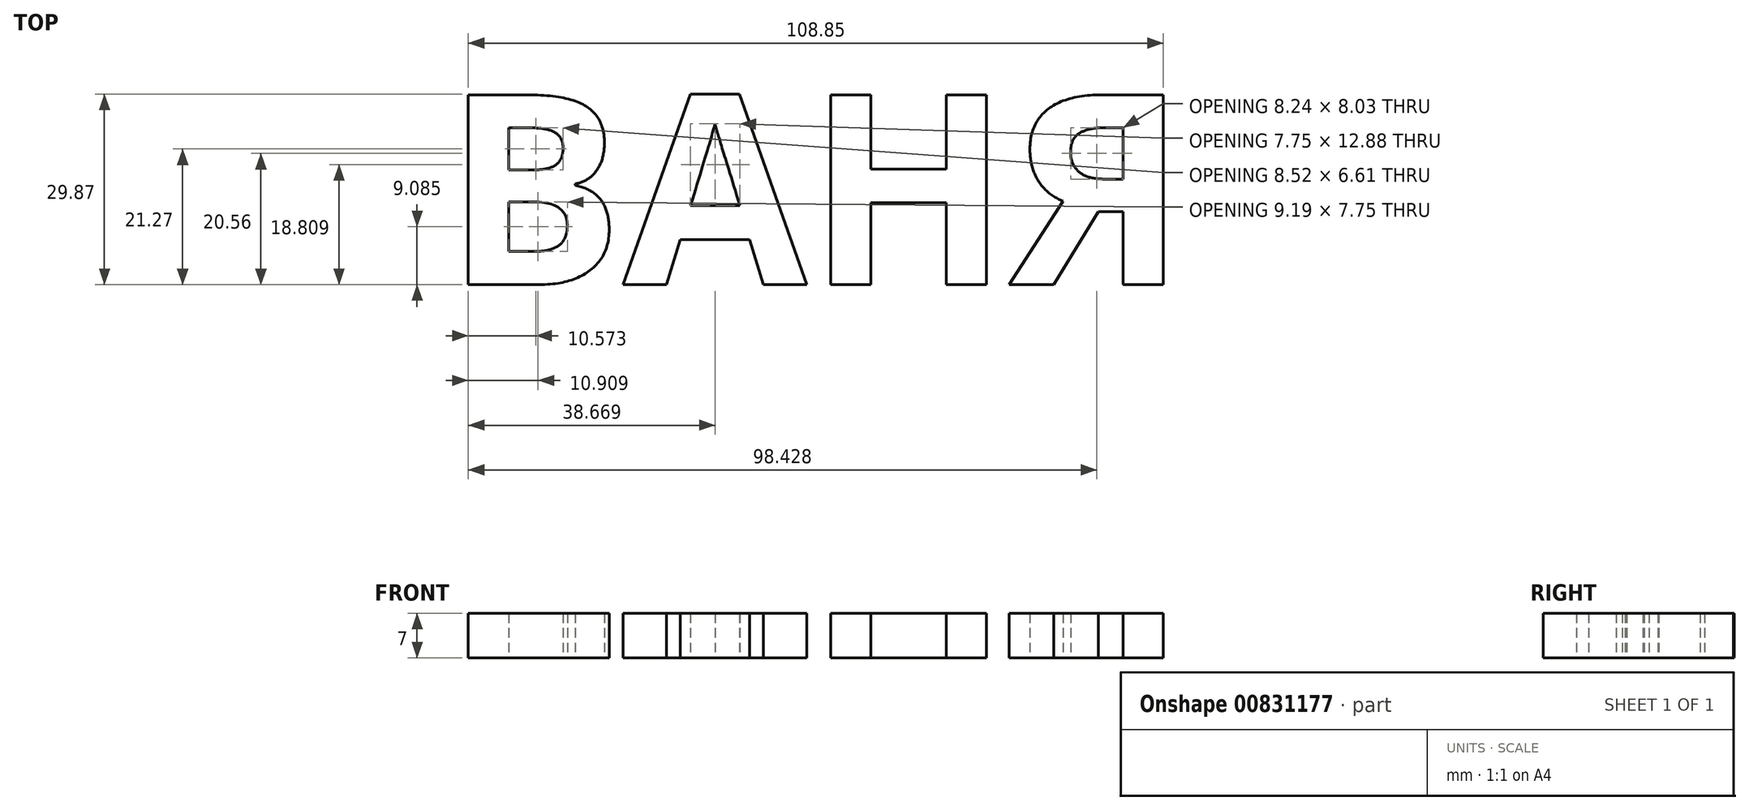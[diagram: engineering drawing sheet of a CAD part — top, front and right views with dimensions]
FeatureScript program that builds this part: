
annotation { "Feature Type Name" : "Feature", "Feature Type Description" : "" }
export const myFeature = defineFeature(function(context is Context, id is Id, definition is map)
    precondition{}
    {
        {
            var Q0;
            Q0=qCreatedBy(makeId("Top.planeOp"),FACE);
            var sketch = newSketch(context, id + "F0", { "sketchPlane" : qUnion([Q0])});
            skText(sketch, "E0", { "text": "ВАНЯ\n", "fontName": "OpenSans-Bold.ttf"});
            const initialGuessF0  = {"E0": [-0.03325, -0.01518, 1, 0, 0.03]};
            skSetInitialGuess(sketch, initialGuessF0);
            skSolve(sketch);
        }
        {
            var Q0;
            Q0=makeQuery(id+"F0.imprint","IMPRINT",FACE,{"disambiguationData":[TD([[makeQuery(id+"F0.imprint","IMPRINT",EDGE,{"derivedFrom":sQuery(id+"F0.wireOp",EDGE,"E0.sketch_text.stroke-49")}),-1.0]])]});
            var Q1;
            Q1=makeQuery(id+"F0.imprint","IMPRINT",FACE,{"disambiguationData":[TD([[makeQuery(id+"F0.imprint","IMPRINT",EDGE,{"derivedFrom":sQuery(id+"F0.wireOp",EDGE,"E0.sketch_text.stroke-37")}),-1.0]])]});
            var Q2;
            Q2=makeQuery(id+"F0.imprint","IMPRINT",FACE,{"disambiguationData":[TD([[makeQuery(id+"F0.imprint","IMPRINT",EDGE,{"derivedFrom":sQuery(id+"F0.wireOp",EDGE,"E0.sketch_text.stroke-25")}),-1.0]])]});
            var Q3;
            Q3=makeQuery(id+"F0.imprint","IMPRINT",FACE,{"disambiguationData":[TD([[makeQuery(id+"F0.imprint","IMPRINT",EDGE,{"derivedFrom":sQuery(id+"F0.wireOp",EDGE,"E0.sketch_text.stroke-0")}),-1.0]])]});
            extrude(context, id + "F1", {"entities" : qUnion([Q0, Q1, Q2, Q3]), "depth" : 7 * mm, "offsetDistance" : 25 * mm});
        }
    });
